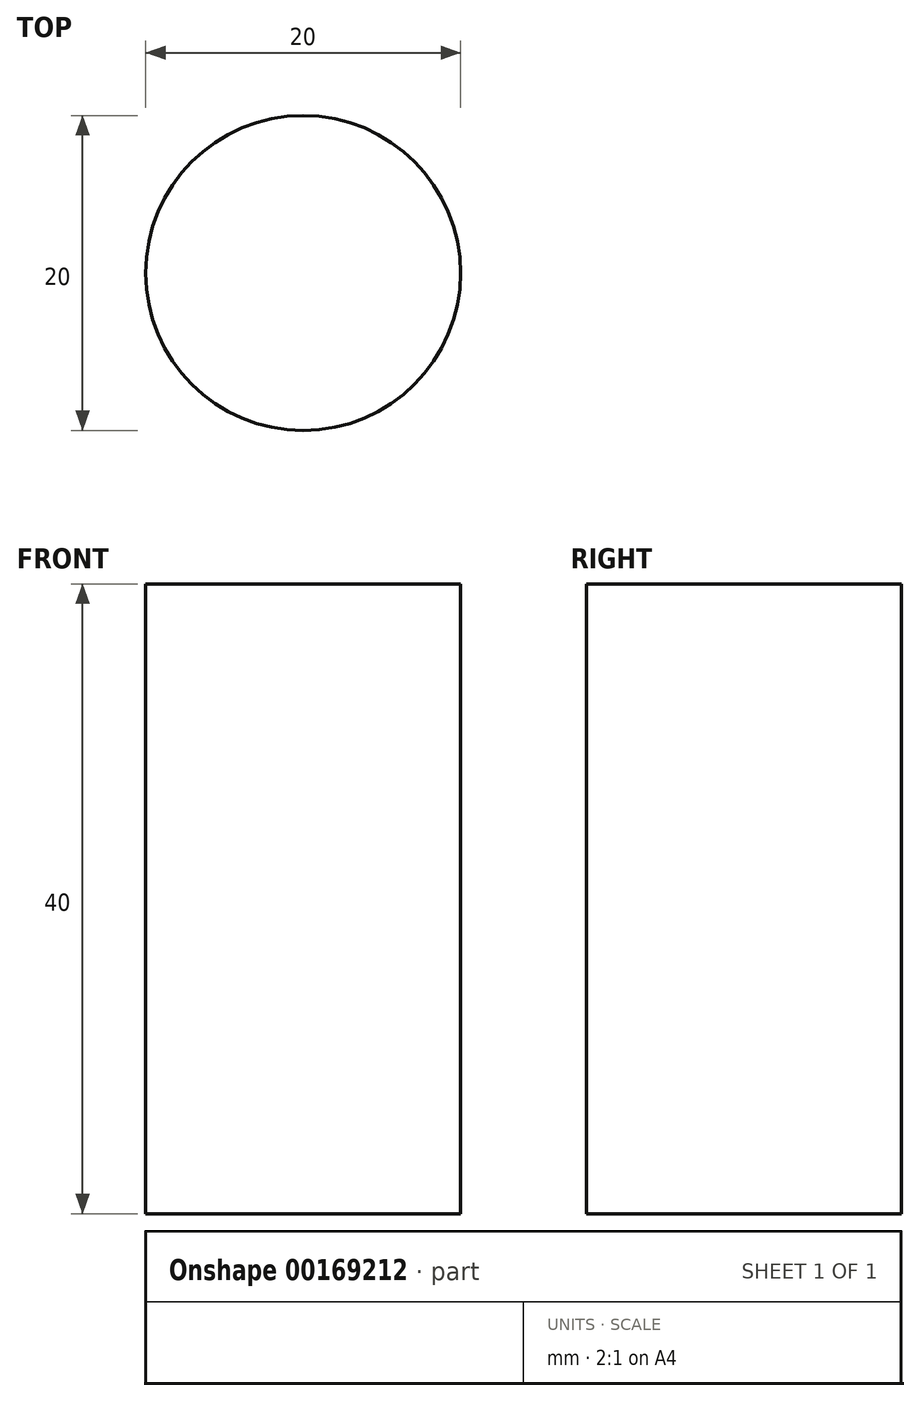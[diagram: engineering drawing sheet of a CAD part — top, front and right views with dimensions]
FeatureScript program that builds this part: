
annotation { "Feature Type Name" : "Feature", "Feature Type Description" : "" }
export const myFeature = defineFeature(function(context is Context, id is Id, definition is map)
    precondition{}
    {
        {
            var Q0;
            Q0=qCreatedBy(makeId("Top.planeOp"),FACE);
            var sketch = newSketch(context, id + "F0", { "sketchPlane" : qUnion([Q0])});
            skCircle(sketch, "E0", {"center": v(0, 0) * mm, "radius": 10 * mm});
            skSolve(sketch);
        }
        {
            var Q0;
            Q0 = qSketchRegion(id + "F0", true);
            extrude(context, id + "F1", {"entities" : qUnion([Q0]), "depth" : 40 * mm});
        }
    });
